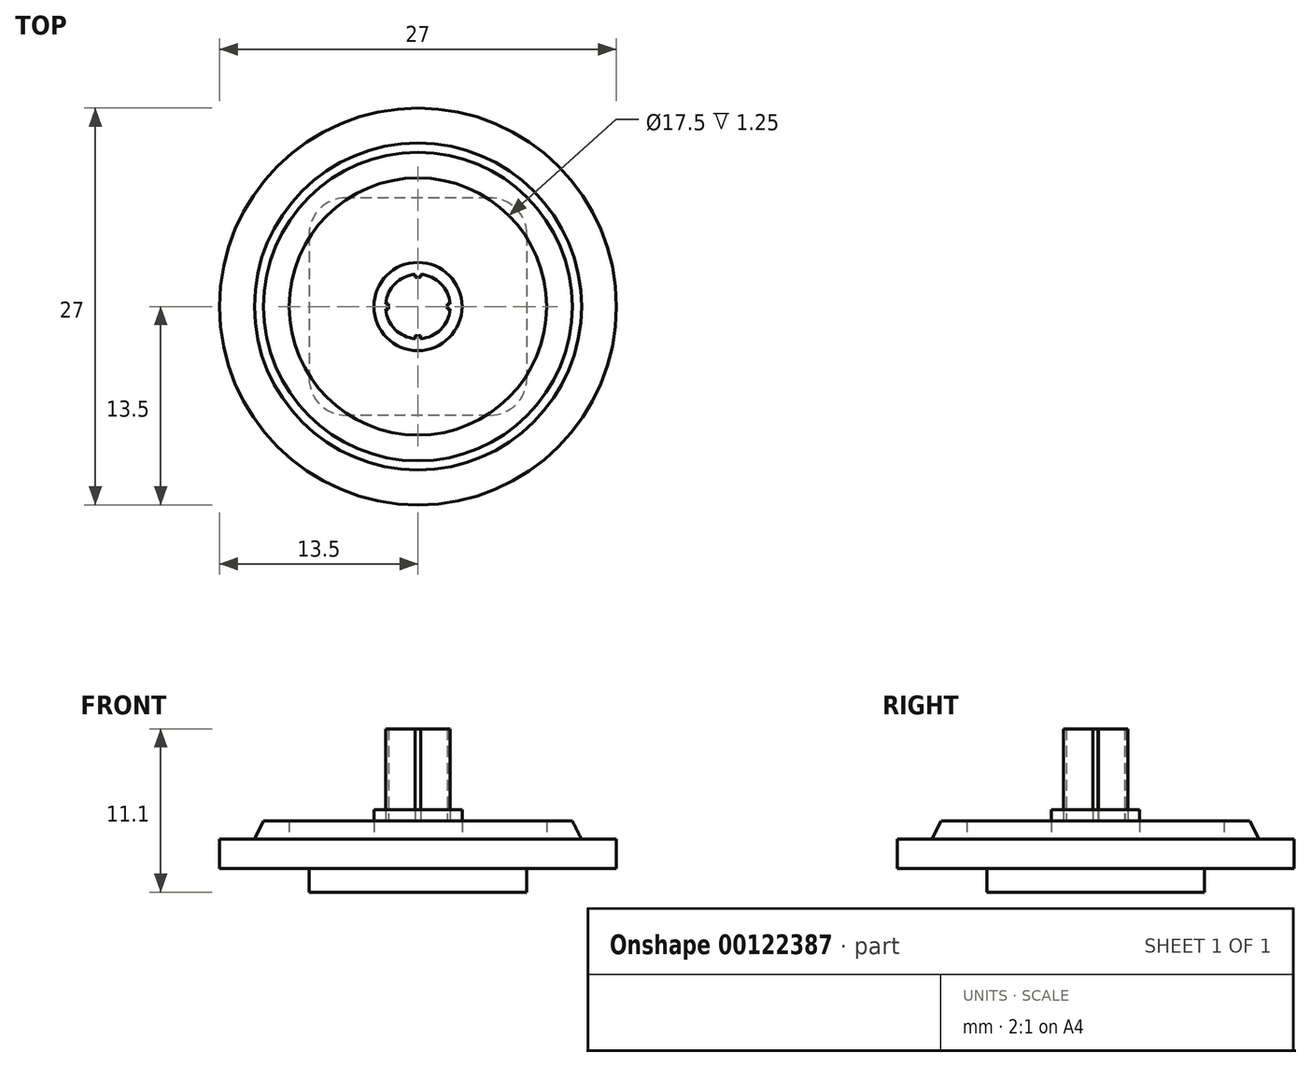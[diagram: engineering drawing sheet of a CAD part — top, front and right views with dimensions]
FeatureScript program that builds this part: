
annotation { "Feature Type Name" : "Feature", "Feature Type Description" : "" }
export const myFeature = defineFeature(function(context is Context, id is Id, definition is map)
    precondition{}
    {
        {
            var Q0;
            Q0=qCreatedBy(makeId("Top.planeOp"),FACE);
            var sketch = newSketch(context, id + "F0", { "sketchPlane" : qUnion([Q0])});
            skCircle(sketch, "E0", {"center": v(0, 0) * mm, "radius": 13.5 * mm});
            skCircle(sketch, "E1", {"center": v(0, 0) * mm, "radius": 11.25 * mm});
            skCircle(sketch, "E2", {"center": v(0, 0) * mm, "radius": 10.5 * mm});
            skCircle(sketch, "E3", {"center": v(0, 0) * mm, "radius": 8.75 * mm});
            skCircle(sketch, "E4", {"center": v(0, 0) * mm, "radius": 3 * mm});
            skCircle(sketch, "E5", {"center": v(0, 0) * mm, "radius": 2.2 * mm});
            skSolve(sketch);
        }
        {
            var Q0;
            Q0=makeQuery(id+"F0.imprint","IMPRINT",FACE,{"disambiguationData":[TD([[makeQuery(id+"F0.imprint","IMPRINT",EDGE,{"derivedFrom":sQuery(id+"F0.wireOp",EDGE,"E4")}),1.0]])]});
            var Q1;
            Q1=makeQuery(id+"F0.imprint","IMPRINT",FACE,{"disambiguationData":[TD([[makeQuery(id+"F0.imprint","IMPRINT",EDGE,{"derivedFrom":sQuery(id+"F0.wireOp",EDGE,"E5")}),1.0]])]});
            var Q2;
            Q2=makeQuery(id+"F0.imprint","IMPRINT",FACE,{"disambiguationData":[TD([[makeQuery(id+"F0.imprint","IMPRINT",EDGE,{"derivedFrom":sQuery(id+"F0.wireOp",EDGE,"E1")}),1.0]])]});
            var Q3;
            Q3=makeQuery(id+"F0.imprint","IMPRINT",FACE,{"disambiguationData":[TD([[makeQuery(id+"F0.imprint","IMPRINT",EDGE,{"derivedFrom":sQuery(id+"F0.wireOp",EDGE,"E0")}),1.0]])]});
            var Q4;
            Q4=makeQuery(id+"F0.imprint","IMPRINT",FACE,{"disambiguationData":[TD([[makeQuery(id+"F0.imprint","IMPRINT",EDGE,{"derivedFrom":sQuery(id+"F0.wireOp",EDGE,"E3")}),1.0]])]});
            var Q5;
            Q5=makeQuery(id+"F0.imprint","IMPRINT",FACE,{"disambiguationData":[TD([[makeQuery(id+"F0.imprint","IMPRINT",EDGE,{"derivedFrom":sQuery(id+"F0.wireOp",EDGE,"E2")}),1.0]])]});
            extrude(context, id + "F1", {"entities" : qUnion([Q0, Q1, Q2, Q3, Q4, Q5]), "oppositeDirection" : true, "depth" : 2 * mm});
        }
        {
            var Q0;
            Q0=makeQuery(id+"F0.imprint","IMPRINT",FACE,{"disambiguationData":[TD([[makeQuery(id+"F0.imprint","IMPRINT",EDGE,{"derivedFrom":sQuery(id+"F0.wireOp",EDGE,"E2")}),1.0]])]});
            cPlane(context, id + "F2", {"entities" : qUnion([Q0]), "cplaneType" : CPlaneType.OFFSET, "offset" : 1.25 * mm, "width" : 150 * mm, "height" : 150 * mm});
        }
        {
            var Q0;
            Q0=qCreatedBy(id+"F2.planeOp",FACE);
            var sketch = newSketch(context, id + "F3", { "sketchPlane" : qUnion([Q0])});
            skCircle(sketch, "E6.0.0", {"center": v(0, 0) * mm, "radius": 10.5 * mm});
            skCircle(sketch, "E7.0", {"center": v(0, 0) * mm, "radius": 8.75 * mm});
            skArc(sketch, "E8.0", {"start": v(-0.18, 2.2) * mm, "mid": v(-1.56, 1.56) * mm, "end": v(-2.2, 0.18) * mm});
            skLineSegment(sketch, "E9.0", {"start": v(0.18, 2) * mm, "end": v(0.18, 2.2) * mm});
            skLineSegment(sketch, "E10.0", {"start": v(-0.18, 2) * mm, "end": v(-0.18, 2.2) * mm});
            skArc(sketch, "E11", {"start": v(2, -0.18) * mm, "mid": v(2, 0) * mm, "end": v(2, 0.18) * mm});
            skLineSegment(sketch, "E12.1.0", {"start": v(-2, -0.18) * mm, "end": v(-2.2, -0.18) * mm});
            skLineSegment(sketch, "E12.1.1", {"start": v(-2, 0.18) * mm, "end": v(-2.2, 0.18) * mm});
            skLineSegment(sketch, "E12.2.0", {"start": v(0.18, -2) * mm, "end": v(0.18, -2.2) * mm});
            skLineSegment(sketch, "E12.2.1", {"start": v(-0.18, -2) * mm, "end": v(-0.18, -2.2) * mm});
            skLineSegment(sketch, "E12.3.0", {"start": v(2, 0.18) * mm, "end": v(2.2, 0.18) * mm});
            skLineSegment(sketch, "E12.3.1", {"start": v(2, -0.18) * mm, "end": v(2.2, -0.18) * mm});
            skArc(sketch, "E13.trimOffspring", {"start": v(2.2, 0.18) * mm, "mid": v(1.56, 1.56) * mm, "end": v(0.18, 2.2) * mm});
            skArc(sketch, "E14.trimOffspring", {"start": v(-2.2, -0.18) * mm, "mid": v(-1.56, -1.56) * mm, "end": v(-0.18, -2.2) * mm});
            skArc(sketch, "E15.trimOffspring", {"start": v(0.18, -2.2) * mm, "mid": v(1.56, -1.56) * mm, "end": v(2.2, -0.18) * mm});
            skArc(sketch, "E16.trimOffspring", {"start": v(-0.18, -2) * mm, "mid": v(0, -2) * mm, "end": v(0.18, -2) * mm});
            skArc(sketch, "E17.trimOffspring", {"start": v(0.18, 2) * mm, "mid": v(0, 2) * mm, "end": v(-0.18, 2) * mm});
            skArc(sketch, "E18.trimOffspring", {"start": v(-2, 0.18) * mm, "mid": v(-2, 0) * mm, "end": v(-2, -0.18) * mm});
            skSolve(sketch);
        }
        {
            var Q0;
            Q0=makeQuery(id+"F0.imprint","IMPRINT",FACE,{"disambiguationData":[TD([[makeQuery(id+"F0.imprint","IMPRINT",EDGE,{"derivedFrom":sQuery(id+"F0.wireOp",EDGE,"E1")}),1.0]])]});
            var Q1;
            Q1=makeQuery(id+"F0.imprint","IMPRINT",FACE,{"disambiguationData":[TD([[makeQuery(id+"F0.imprint","IMPRINT",EDGE,{"derivedFrom":sQuery(id+"F0.wireOp",EDGE,"E2")}),1.0]])]});
            extrude(context, id + "F4", {"entities" : qUnion([Q0, Q1]), "operationType" : NewBodyOperationType.ADD, "depth" : 1.25 * mm});
        }
        {
            var Q0;
            Q0=makeQuery(id+"F4.opExtrude","CAP_EDGE",EDGE,{"disambiguationData":[OSD([sQuery(id+"F0.wireOp",EDGE,"E1")])],"isStart":false});
            chamfer(context, id + "F5", {"entities" : qUnion([Q0]), "chamferType" : ChamferType.TWO_OFFSETS, "width1" : 1.5 * mm, "oppositeDirection" : true, "width2" : .75 * mm, "tangentPropagation" : true});
        }
        {
            var Q0;
            Q0=makeQuery(id+"F0.imprint","IMPRINT",FACE,{"disambiguationData":[TD([[makeQuery(id+"F0.imprint","IMPRINT",EDGE,{"derivedFrom":sQuery(id+"F0.wireOp",EDGE,"E4")}),1.0]])]});
            extrude(context, id + "F6", {"entities" : qUnion([Q0]), "operationType" : NewBodyOperationType.ADD, "depth" : 2 * mm});
        }
        {
            var Q0;
            Q0=makeQuery(id+"F0.imprint","IMPRINT",FACE,{"disambiguationData":[TD([[makeQuery(id+"F0.imprint","IMPRINT",EDGE,{"derivedFrom":sQuery(id+"F0.wireOp",EDGE,"E5")}),1.0]])]});
            extrude(context, id + "F7", {"entities" : qUnion([Q0]), "operationType" : NewBodyOperationType.ADD, "depth" : 2 * mm});
        }
        {
            var Q0;
            Q0=makeQuery(id+"F3.imprint","IMPRINT",FACE,{"disambiguationData":[TD([[makeQuery(id+"F3.imprint","IMPRINT",EDGE,{"derivedFrom":sQuery(id+"F3.wireOp",EDGE,"E8.0")}),1.0]])]});
            extrude(context, id + "F8", {"entities" : qUnion([Q0]), "depth" : 6.25 * mm});
        }
        {
            var Q0;
            Q0=makeQuery(id+"F1.opExtrude","CAP_FACE",FACE,{"disambiguationData":[OSD([sQuery(id+"F0.wireOp",EDGE,"E0")])],"isStart":false});
            cPlane(context, id + "F9", {"entities" : qUnion([Q0]), "cplaneType" : CPlaneType.OFFSET, "offset" : 0 * mm, "width" : 150 * mm, "height" : 150 * mm});
        }
        {
            var Q0;
            Q0=qCreatedBy(id+"F9.planeOp",FACE);
            var sketch = newSketch(context, id + "F10", { "sketchPlane" : qUnion([Q0])});
            skLineSegment(sketch, "E19.bottom", {"start": v(4.9, -7.4) * mm, "end": v(-4.9, -7.4) * mm});
            skLineSegment(sketch, "E19.top", {"start": v(4.9, 7.4) * mm, "end": v(-4.9, 7.4) * mm});
            skLineSegment(sketch, "E19.left", {"start": v(7.4, -4.9) * mm, "end": v(7.4, 4.9) * mm});
            skLineSegment(sketch, "E19.right", {"start": v(-7.4, -4.9) * mm, "end": v(-7.4, 4.9) * mm});
            skPoint(sketch, "E19.middle", {"position": v(0, 0) * mm});
            skPoint(sketch, "E20.visualSharp", {"position": v(-7.4, 7.4) * mm});
            skArc(sketch, "E20.filletArc", {"start": v(-4.9, 7.4) * mm, "mid": v(-6.67, 6.67) * mm, "end": v(-7.4, 4.9) * mm});
            skPoint(sketch, "E21.visualSharp", {"position": v(7.4, 7.4) * mm});
            skArc(sketch, "E21.filletArc", {"start": v(7.4, 4.9) * mm, "mid": v(6.67, 6.67) * mm, "end": v(4.9, 7.4) * mm});
            skPoint(sketch, "E22.visualSharp", {"position": v(7.4, -7.4) * mm});
            skArc(sketch, "E22.filletArc", {"start": v(4.9, -7.4) * mm, "mid": v(6.67, -6.67) * mm, "end": v(7.4, -4.9) * mm});
            skPoint(sketch, "E23.visualSharp", {"position": v(-7.4, -7.4) * mm});
            skArc(sketch, "E23.filletArc", {"start": v(-7.4, -4.9) * mm, "mid": v(-6.67, -6.67) * mm, "end": v(-4.9, -7.4) * mm});
            skSolve(sketch);
        }
        {
            var Q0;
            Q0=makeQuery(id+"F10.imprint","IMPRINT",FACE,{"disambiguationData":[TD([[makeQuery(id+"F10.imprint","IMPRINT",EDGE,{"derivedFrom":sQuery(id+"F10.wireOp",EDGE,"E19.bottom")}),-1.0]])]});
            extrude(context, id + "F11", {"entities" : qUnion([Q0]), "operationType" : NewBodyOperationType.ADD, "depth" : 1.6 * mm});
        }
    });
